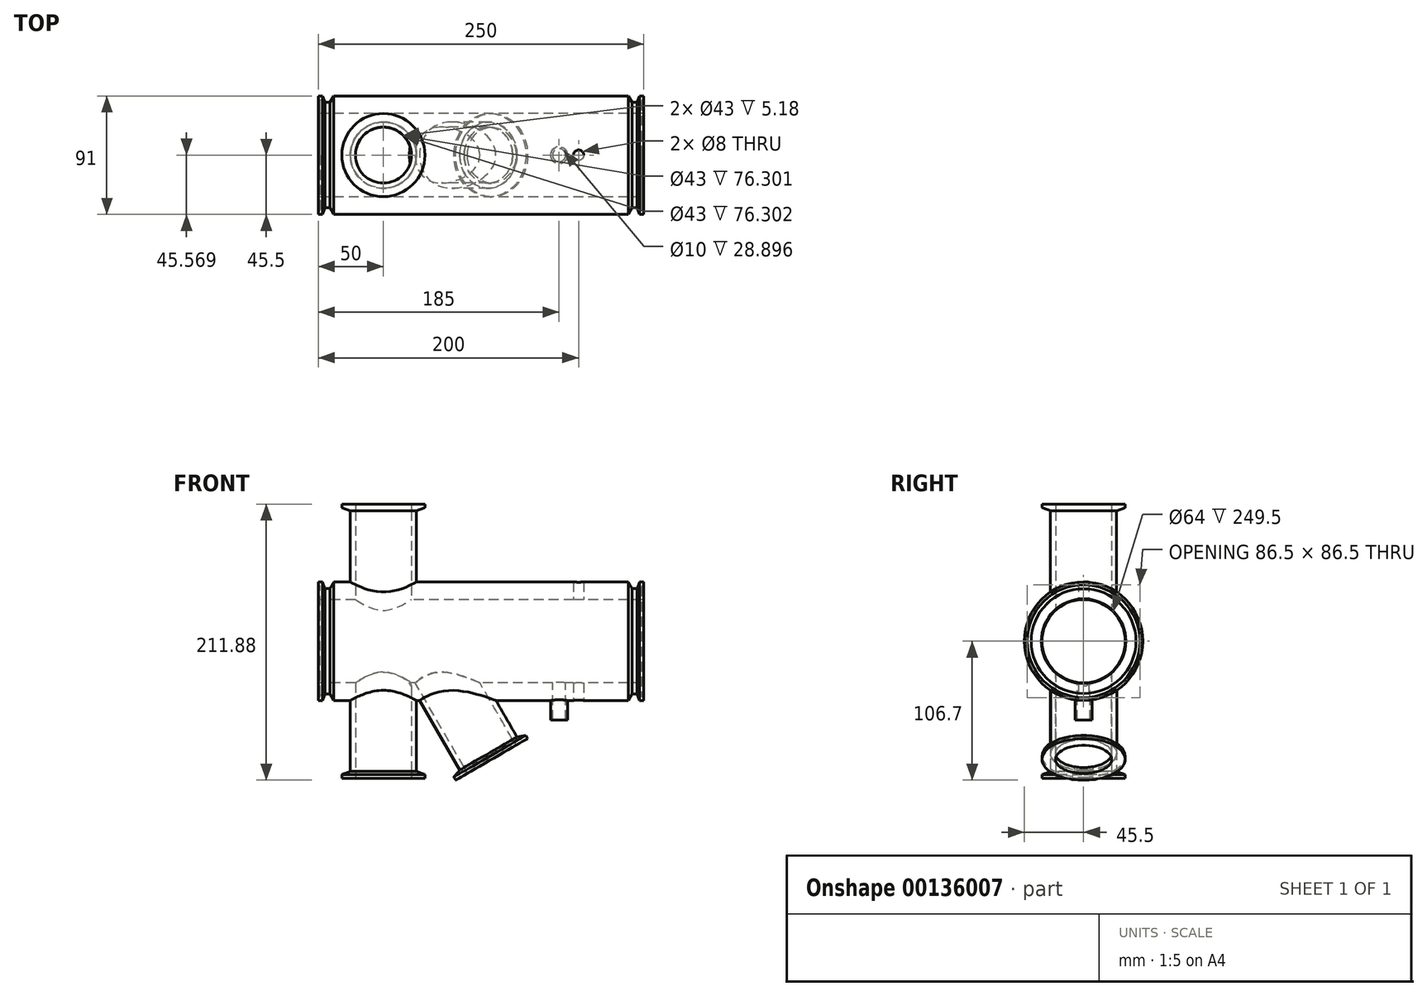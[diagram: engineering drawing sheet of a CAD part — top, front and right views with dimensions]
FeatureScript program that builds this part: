
annotation { "Feature Type Name" : "Feature", "Feature Type Description" : "" }
export const myFeature = defineFeature(function(context is Context, id is Id, definition is map)
    precondition{}
    {
        {
            var Q0;
            Q0=qCreatedBy(makeId("Top.planeOp"),FACE);
            var sketch = newSketch(context, id + "F0", { "sketchPlane" : qUnion([Q0])});
            skCircle(sketch, "E0", {"center": v(0, 0) * mm, "radius": 21.5 * mm});
            skCircle(sketch, "E1", {"center": v(0, 0) * mm, "radius": 25.4 * mm});
            skSolve(sketch);
        }
        {
            var Q0;
            Q0 = qSketchRegion(id + "F0", true);
            extrude(context, id + "F1", {"entities" : qUnion([Q0]), "depth" : 100 * mm});
        }
        {
            var Q0;
            Q0=qCreatedBy(makeId("Right.planeOp"),FACE);
            var sketch = newSketch(context, id + "F2", { "sketchPlane" : qUnion([Q0])});
            skCircle(sketch, "E2", {"center": v(0, 0) * mm, "radius": 32 * mm});
            skCircle(sketch, "E3", {"center": v(0, 0) * mm, "radius": 45.5 * mm});
            skSolve(sketch);
        }
        {
            var Q0;
            Q0 = qSketchRegion(id + "F2", true);
            extrude(context, id + "F3", {"entities" : qUnion([Q0]), "operationType" : NewBodyOperationType.ADD, "depth" : 200 * mm});
        }
        {
            var Q0;
            Q0=qCreatedBy(makeId("Top.planeOp"),FACE);
            var sketch = newSketch(context, id + "F4", { "sketchPlane" : qUnion([Q0])});
            skLineSegment(sketch, "E4", {"start": v(0, -75.06) * mm, "end": v(0, 75.06) * mm, "construction": true});
            skSolve(sketch);
        }
        {
            var Q0;
            Q0=sQuery(id+"F4.wireOp",EDGE,"E4");
            cPlane(context, id + "F5", {"entities" : qUnion([Q0]), "cplaneType" : CPlaneType.LINE_ANGLE, "offset" : 25 * mm, "angle" : 0 * degree, "width" : 150 * mm, "height" : 150 * mm});
        }
        {
            var Q0;
            Q0=qCreatedBy(id+"F5.planeOp",FACE);
            var sketch = newSketch(context, id + "F6", { "sketchPlane" : qUnion([Q0])});
            skCircle(sketch, "E5", {"center": v(0, 0) * mm, "radius": 21.5 * mm});
            skCircle(sketch, "E6", {"center": v(0, 0) * mm, "radius": 25.4 * mm});
            skSolve(sketch);
        }
        {
            var Q0;
            Q0 = qSketchRegion(id + "F6", true);
            extrude(context, id + "F7", {"entities" : qUnion([Q0]), "operationType" : NewBodyOperationType.ADD, "oppositeDirection" : true, "depth" : 100 * mm});
        }
        {
            var Q0;
            Q0=sQuery(id+"F4.wireOp",EDGE,"E4");
            var Q1;
            Q1=qCreatedBy(makeId("Top.planeOp"),FACE);
            cPlane(context, id + "F8", {"entities" : qUnion([Q0, Q1]), "cplaneType" : CPlaneType.LINE_ANGLE, "offset" : 25 * mm, "angle" : 150 * degree, "width" : 150 * mm, "height" : 150 * mm});
        }
        {
            var Q0;
            Q0=qCreatedBy(id+"F8.planeOp",FACE);
            cPlane(context, id + "F9", {"entities" : qUnion([Q0]), "cplaneType" : CPlaneType.OFFSET, "offset" : 30 * mm, "oppositeDirection" : true, "width" : 150 * mm, "height" : 150 * mm});
        }
        {
            var Q0;
            Q0=qCreatedBy(makeId("Top.planeOp"),FACE);
            cPlane(context, id + "F10", {"entities" : qUnion([Q0]), "cplaneType" : CPlaneType.OFFSET, "offset" : 200 * mm, "width" : 150 * mm, "height" : 150 * mm});
        }
        {
            var Q0;
            Q0=qCreatedBy(id+"F10.planeOp",FACE);
            var sketch = newSketch(context, id + "F11", { "sketchPlane" : qUnion([Q0])});
            skCircle(sketch, "E7.0", {"center": v(0, 0) * mm, "radius": 21.5 * mm});
            skSolve(sketch);
        }
        {
            var Q0;
            Q0=qCreatedBy(makeId("Right.planeOp"),FACE);
            cPlane(context, id + "F12", {"entities" : qUnion([Q0]), "cplaneType" : CPlaneType.OFFSET, "offset" : 200 * mm, "width" : 150 * mm, "height" : 150 * mm});
        }
        {
            var Q0;
            Q0=qCreatedBy(id+"F12.planeOp",FACE);
            var sketch = newSketch(context, id + "F13", { "sketchPlane" : qUnion([Q0])});
            skCircle(sketch, "E8.0", {"center": v(0, 0) * mm, "radius": 32 * mm});
            skSolve(sketch);
        }
        {
            var Q0;
            Q0=qCreatedBy(id+"F9.planeOp",FACE);
            cPlane(context, id + "F14", {"entities" : qUnion([Q0]), "cplaneType" : CPlaneType.OFFSET, "offset" : 150 * mm, "oppositeDirection" : true, "width" : 150 * mm, "height" : 150 * mm});
        }
        {
            var Q0;
            Q0=qCreatedBy(id+"F5.planeOp",FACE);
            cPlane(context, id + "F15", {"entities" : qUnion([Q0]), "cplaneType" : CPlaneType.OFFSET, "offset" : 150 * mm, "oppositeDirection" : true, "width" : 150 * mm, "height" : 150 * mm});
        }
        {
            var Q0;
            Q0=qCreatedBy(id+"F15.planeOp",FACE);
            var sketch = newSketch(context, id + "F16", { "sketchPlane" : qUnion([Q0])});
            skCircle(sketch, "E9.0", {"center": v(0, 0) * mm, "radius": 21.5 * mm});
            skSolve(sketch);
        }
        {
            var Q0;
            Q0=qCreatedBy(makeId("Right.planeOp"),FACE);
            var sketch = newSketch(context, id + "F17", { "sketchPlane" : qUnion([Q0])});
            skCircle(sketch, "E10", {"center": v(0, 0) * mm, "radius": 32 * mm});
            skCircle(sketch, "E11", {"center": v(0, 0) * mm, "radius": 45.5 * mm});
            skSolve(sketch);
        }
        {
            var Q0;
            Q0 = qSketchRegion(id + "F17", true);
            extrude(context, id + "F18", {"entities" : qUnion([Q0]), "operationType" : NewBodyOperationType.ADD, "oppositeDirection" : true, "depth" : 50 * mm});
        }
        {
            var Q0;
            Q0=makeQuery(id+"F18.opExtrude","CAP_FACE",FACE,{"disambiguationData":[OSD([sQuery(id+"F17.wireOp",EDGE,"E10"),sQuery(id+"F17.wireOp",EDGE,"E11")])],"isStart":false});
            var sketch = newSketch(context, id + "F19", { "sketchPlane" : qUnion([Q0])});
            skCircle(sketch, "E12", {"center": v(0, 0) * mm, "radius": 32 * mm});
            skSolve(sketch);
        }
        {
            var Q0;
            Q0 = qSketchRegion(id + "F16", true);
            extrude(context, id + "F20", {"entities" : qUnion([Q0]), "operationType" : NewBodyOperationType.REMOVE, "depth" : 150 * mm});
        }
        {
            var Q0;
            Q0 = qSketchRegion(id + "F11", true);
            extrude(context, id + "F21", {"entities" : qUnion([Q0]), "operationType" : NewBodyOperationType.REMOVE, "oppositeDirection" : true, "depth" : 202.66 * mm});
        }
        {
            var Q0;
            Q0=qCreatedBy(makeId("Front.planeOp"),FACE);
            var sketch = newSketch(context, id + "F22", { "sketchPlane" : qUnion([Q0])});
            skLineSegment(sketch, "E13", {"start": v(0, 0) * mm, "end": v(200, 0) * mm, "construction": true});
            skLineSegment(sketch, "E14", {"start": v(200, 0) * mm, "end": v(200, 45.5) * mm, "construction": true});
            skLineSegment(sketch, "E15", {"start": v(200, 45.5) * mm, "end": v(196.8, 45.5) * mm, "construction": true});
            skLineSegment(sketch, "E16", {"start": v(196.8, 45.5) * mm, "end": v(194.97, 40.48) * mm});
            skLineSegment(sketch, "E17", {"start": v(194.97, 40.48) * mm, "end": v(190.97, 40.48) * mm});
            skLineSegment(sketch, "E18", {"start": v(190.97, 40.48) * mm, "end": v(188.08, 45.5) * mm});
            skLineSegment(sketch, "E19", {"start": v(188.08, 45.5) * mm, "end": v(196.8, 45.5) * mm});
            skLineSegment(sketch, "E20", {"start": v(200, 0) * mm, "end": v(-50, 0) * mm, "construction": true});
            skLineSegment(sketch, "E21", {"start": v(75, 0) * mm, "end": v(75, 86.7) * mm, "construction": true});
            skPoint(sketch, "E21.endSnap0", {"position": v(75, 0) * mm});
            skLineSegment(sketch, "E22.MirrorCS", {"start": v(-40.97, 40.48) * mm, "end": v(-38.08, 45.5) * mm});
            skLineSegment(sketch, "E23.MirrorCS", {"start": v(-38.08, 45.5) * mm, "end": v(-46.8, 45.5) * mm});
            skLineSegment(sketch, "E24.MirrorCS", {"start": v(-44.97, 40.48) * mm, "end": v(-40.97, 40.48) * mm});
            skLineSegment(sketch, "E25.MirrorCS", {"start": v(-46.8, 45.5) * mm, "end": v(-44.97, 40.48) * mm});
            skCircle(sketch, "E26", {"center": v(200, 41.75) * mm, "radius": 1.5 * mm});
            skCircle(sketch, "E27", {"center": v(-50.02, 41.75) * mm, "radius": 1.5 * mm});
            skSolve(sketch);
        }
        {
            var Q0;
            Q0 = qSketchRegion(id + "F22", true);
            var Q1;
            Q1=sQuery(id+"F22.wireOp",EDGE,"E13");
            revolve(context, id + "F23", {"operationType" : NewBodyOperationType.REMOVE, "entities" : qUnion([Q0]), "axis" : qUnion([Q1]), "revolveType" : RevolveType.FULL});
        }
        {
            var Q0;
            Q0=qCreatedBy(makeId("Top.planeOp"),FACE);
            var sketch = newSketch(context, id + "F24", { "sketchPlane" : qUnion([Q0])});
            skCircle(sketch, "E28", {"center": v(135, 0) * mm, "radius": 5 * mm});
            skSolve(sketch);
        }
        {
            var Q0;
            Q0 = qSketchRegion(id + "F24", true);
            extrude(context, id + "F25", {"entities" : qUnion([Q0]), "operationType" : NewBodyOperationType.REMOVE, "oppositeDirection" : true, "depth" : 51.26 * mm});
        }
        {
            var Q0;
            Q0=qCreatedBy(id+"F9.planeOp",FACE);
            var sketch = newSketch(context, id + "F26", { "sketchPlane" : qUnion([Q0])});
            skLineSegment(sketch, "E29", {"start": v(-16.86, 0.07) * mm, "end": v(164.96, 0.07) * mm, "construction": true});
            skSolve(sketch);
        }
        {
            var Q0;
            Q0=qCreatedBy(id+"F9.planeOp",FACE);
            var sketch = newSketch(context, id + "F27", { "sketchPlane" : qUnion([Q0])});
            skLineSegment(sketch, "E30.0", {"start": v(-16.86, 0.07) * mm, "end": v(164.96, 0.07) * mm, "construction": true});
            skCircle(sketch, "E31", {"center": v(26.7, 0.07) * mm, "radius": 21.5 * mm});
            skCircle(sketch, "E32", {"center": v(26.7, 0.07) * mm, "radius": 25.4 * mm});
            skSolve(sketch);
        }
        {
            var Q0;
            Q0 = qSketchRegion(id + "F27", true);
            extrude(context, id + "F28", {"entities" : qUnion([Q0]), "operationType" : NewBodyOperationType.ADD, "oppositeDirection" : true, "depth" : 85 * mm});
        }
        {
            var Q0;
            Q0=qCreatedBy(id+"F14.planeOp",FACE);
            var sketch = newSketch(context, id + "F29", { "sketchPlane" : qUnion([Q0])});
            skCircle(sketch, "E33.0", {"center": v(26.7, 0.07) * mm, "radius": 21.5 * mm});
            skSolve(sketch);
        }
        {
            var Q0;
            Q0 = qSketchRegion(id + "F29", true);
            extrude(context, id + "F30", {"entities" : qUnion([Q0]), "operationType" : NewBodyOperationType.REMOVE, "depth" : 150 * mm});
        }
        {
            var Q0;
            Q0 = qSketchRegion(id + "F13", true);
            extrude(context, id + "F31", {"entities" : qUnion([Q0]), "operationType" : NewBodyOperationType.REMOVE, "oppositeDirection" : true, "depth" : 250 * mm});
        }
        {
            var Q0;
            Q0=qCreatedBy(makeId("Right.planeOp"),FACE);
            var sketch = newSketch(context, id + "F32", { "sketchPlane" : qUnion([Q0])});
            skLineSegment(sketch, "E34", {"start": v(0.07, 0.29) * mm, "end": v(0.07, 100) * mm, "construction": true});
            skLineSegment(sketch, "E35", {"start": v(-21.43, 105.18) * mm, "end": v(-31.87, 105.18) * mm});
            skLineSegment(sketch, "E36", {"start": v(-31.87, 105.18) * mm, "end": v(-31.87, 102.94) * mm});
            skLineSegment(sketch, "E37", {"start": v(-31.34, 102.19) * mm, "end": v(-25.33, 100) * mm});
            skLineSegment(sketch, "E38", {"start": v(0.07, 100) * mm, "end": v(0.07, 105.18) * mm});
            skPoint(sketch, "E39.visualSharp", {"position": v(-31.87, 102.38) * mm});
            skArc(sketch, "E39.filletArc", {"start": v(-31.87, 102.94) * mm, "mid": v(-31.73, 102.48) * mm, "end": v(-31.34, 102.19) * mm});
            skLineSegment(sketch, "E40", {"start": v(-21.43, 105.18) * mm, "end": v(-21.43, 100) * mm});
            skLineSegment(sketch, "E41.trimOffspring", {"start": v(0.07, 105.18) * mm, "end": v(0.07, 132.96) * mm, "construction": true});
            skPoint(sketch, "E42.visualSharp", {"position": v(-25.33, 100) * mm});
            skLineSegment(sketch, "E43", {"start": v(-21.43, 100) * mm, "end": v(-25.33, 100) * mm});
            skLineSegment(sketch, "E44", {"start": v(-21.43, -100) * mm, "end": v(-25.33, -100) * mm});
            skLineSegment(sketch, "E45", {"start": v(0.07, 0.29) * mm, "end": v(0.07, -105.38) * mm});
            skLineSegment(sketch, "E46", {"start": v(-21.43, -100) * mm, "end": v(-21.43, -105.18) * mm});
            skLineSegment(sketch, "E47", {"start": v(-21.43, -105.18) * mm, "end": v(-31.87, -105.18) * mm});
            skPoint(sketch, "E48.orphan", {"position": v(-50.73, -100) * mm});
            skPoint(sketch, "E49.orphan", {"position": v(0.07, -100) * mm});
            skLineSegment(sketch, "E50", {"start": v(-25.33, -100) * mm, "end": v(-31.87, -102.38) * mm});
            skLineSegment(sketch, "E51", {"start": v(-31.87, -102.38) * mm, "end": v(-31.87, -105.18) * mm});
            skSolve(sketch);
        }
        {
            var Q0;
            Q0 = qSketchRegion(id + "F32", true);
            var Q1;
            Q1=sQuery(id+"F32.wireOp",EDGE,"E34");
            revolve(context, id + "F33", {"operationType" : NewBodyOperationType.ADD, "entities" : qUnion([Q0]), "axis" : qUnion([Q1]), "revolveType" : RevolveType.FULL});
        }
        {
            var Q0;
            Q0=qCreatedBy(makeId("Front.planeOp"),FACE);
            var sketch = newSketch(context, id + "F34", { "sketchPlane" : qUnion([Q0])});
            skLineSegment(sketch, "E52", {"start": v(80.62, -86.24) * mm, "end": v(62.95, -55.63) * mm, "construction": true});
            skLineSegment(sketch, "E53.0", {"start": v(58.62, -98.94) * mm, "end": v(102.62, -73.54) * mm, "construction": true});
            skLineSegment(sketch, "E54", {"start": v(102.62, -73.54) * mm, "end": v(109.47, -72.34) * mm});
            skLineSegment(sketch, "E55", {"start": v(109.47, -72.34) * mm, "end": v(110.87, -74.76) * mm});
            skLineSegment(sketch, "E56", {"start": v(110.87, -74.76) * mm, "end": v(101.83, -79.98) * mm});
            skLineSegment(sketch, "E57", {"start": v(101.83, -79.98) * mm, "end": v(99.24, -75.5) * mm});
            skLineSegment(sketch, "E58", {"start": v(102.62, -73.54) * mm, "end": v(99.24, -75.5) * mm});
            skSolve(sketch);
        }
        {
            var Q0;
            Q0 = qSketchRegion(id + "F34", true);
            var Q1;
            Q1=sQuery(id+"F34.wireOp",EDGE,"E52");
            revolve(context, id + "F35", {"operationType" : NewBodyOperationType.ADD, "entities" : qUnion([Q0]), "axis" : qUnion([Q1]), "revolveType" : RevolveType.FULL});
        }
        {
            var Q0;
            Q0=qCreatedBy(makeId("Top.planeOp"),FACE);
            cPlane(context, id + "F36", {"entities" : qUnion([Q0]), "cplaneType" : CPlaneType.OFFSET, "offset" : 45.5 * mm, "oppositeDirection" : true, "width" : 150 * mm, "height" : 150 * mm});
        }
        {
            var Q0;
            Q0=qCreatedBy(id+"F36.planeOp",FACE);
            var sketch = newSketch(context, id + "F37", { "sketchPlane" : qUnion([Q0])});
            skCircle(sketch, "E59.0", {"center": v(135, 0) * mm, "radius": 5 * mm});
            skCircle(sketch, "E60", {"center": v(135, 0) * mm, "radius": 6.5 * mm});
            skSolve(sketch);
        }
        {
            var Q0;
            Q0 = qSketchRegion(id + "F37", true);
            extrude(context, id + "F38", {"entities" : qUnion([Q0]), "operationType" : NewBodyOperationType.ADD, "depth" : 5 * mm, "hasSecondDirection" : true, "secondDirectionOppositeDirection" : true, "secondDirectionDepth" : 15 * mm});
        }
        {
            var Q0;
            Q0=qCreatedBy(id+"F36.planeOp",FACE);
            var sketch = newSketch(context, id + "F39", { "sketchPlane" : qUnion([Q0])});
            skCircle(sketch, "E61", {"center": v(150, 0) * mm, "radius": 4 * mm});
            skSolve(sketch);
        }
        {
            var Q0;
            Q0 = qSketchRegion(id + "F39", true);
            extrude(context, id + "F40", {"entities" : qUnion([Q0]), "operationType" : NewBodyOperationType.REMOVE, "endBound" : BoundingType.THROUGH_ALL, "depth" : 25 * mm});
        }
        {
            var Q0;
            Q0=makeQuery(id+"F3.opExtrude","CAP_EDGE",EDGE,{"disambiguationData":[OSD([sQuery(id+"F2.wireOp",EDGE,"E2")])],"isStart":false});
            chamfer(context, id + "F41", {"entities" : qUnion([Q0]), "width" : 0.5 * mm, "tangentPropagation" : true});
        }
    });
